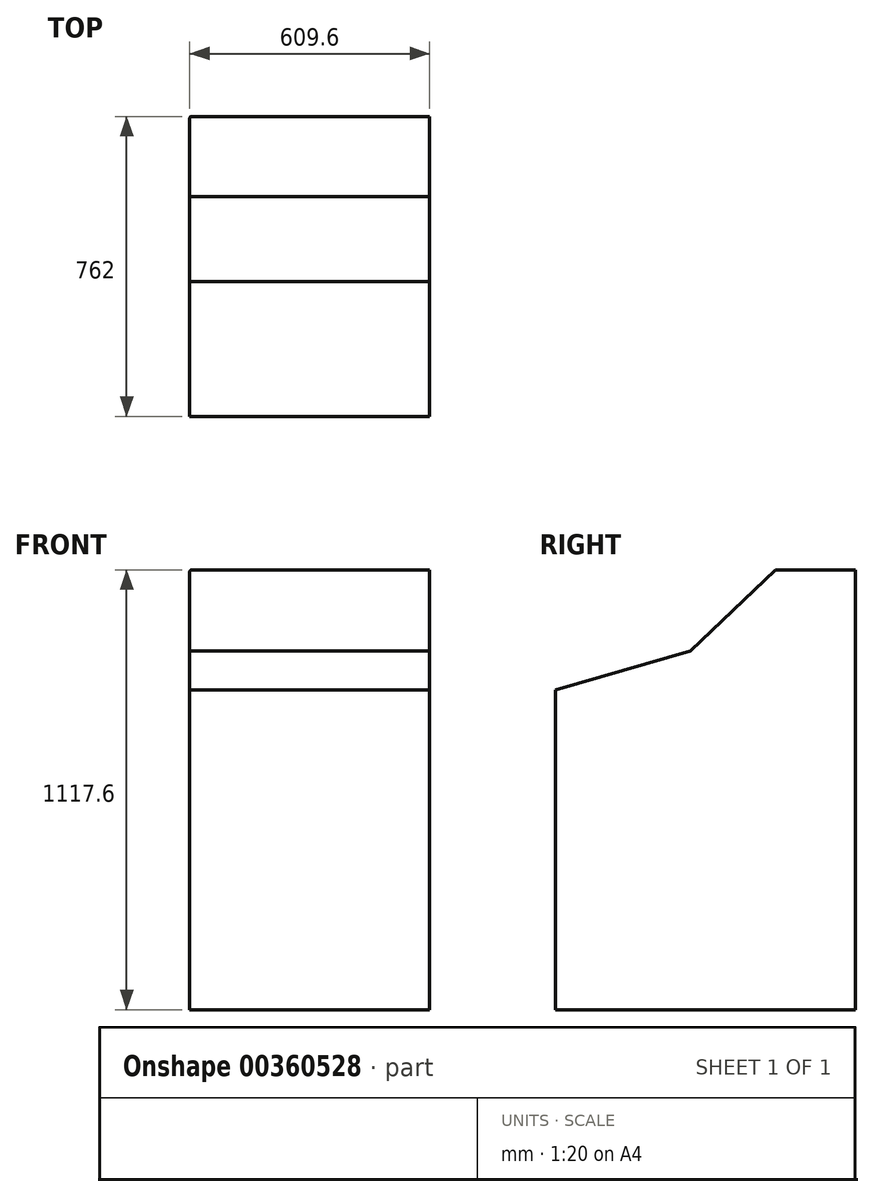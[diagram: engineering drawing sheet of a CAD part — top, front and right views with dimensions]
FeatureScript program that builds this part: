
annotation { "Feature Type Name" : "Feature", "Feature Type Description" : "" }
export const myFeature = defineFeature(function(context is Context, id is Id, definition is map)
    precondition{}
    {
        {
            var Q0;
            Q0=qCreatedBy(makeId("Right.planeOp"),FACE);
            var sketch = newSketch(context, id + "F0", { "sketchPlane" : qUnion([Q0])});
            skLineSegment(sketch, "E0", {"start": v(268.6, -659.9) * mm, "end": v(268.6, 457.7) * mm});
            skLineSegment(sketch, "E1", {"start": v(268.6, 457.7) * mm, "end": v(65.4, 457.7) * mm});
            skLineSegment(sketch, "E2", {"start": v(268.6, -659.9) * mm, "end": v(-493.4, -659.9) * mm});
            skLineSegment(sketch, "E3", {"start": v(-493.4, -659.9) * mm, "end": v(-493.4, 152.9) * mm});
            skLineSegment(sketch, "E4", {"start": v(-493.4, 152.9) * mm, "end": v(-151.71, 251.4) * mm});
            skLineSegment(sketch, "E5", {"start": v(-151.71, 251.4) * mm, "end": v(65.4, 457.7) * mm});
            skSolve(sketch);
        }
        {
            var Q0;
            Q0 = qSketchRegion(id + "F0", true);
            extrude(context, id + "F1", {"entities" : qUnion([Q0]), "endBound" : BoundingType.SYMMETRIC, "depth" : 609.6 * mm});
        }
        {
            var Q0;
            Q0=makeQuery(id+"F1.opExtrude","CAP_EDGE",EDGE,{"disambiguationData":[OSD([sQuery(id+"F0.wireOp",EDGE,"E1")])],"isStart":true});
            var Q1;
            Q1=makeQuery(id+"F1.opExtrude","CAP_EDGE",EDGE,{"disambiguationData":[OSD([sQuery(id+"F0.wireOp",EDGE,"E0")])],"isStart":true});
            fillet(context, id + "F2", {"entities" : qUnion([Q0, Q1]), "radius" : 4.57 * mm, "tangentPropagation" : true, "allowEdgeOverflow" : false});
        }
    });
